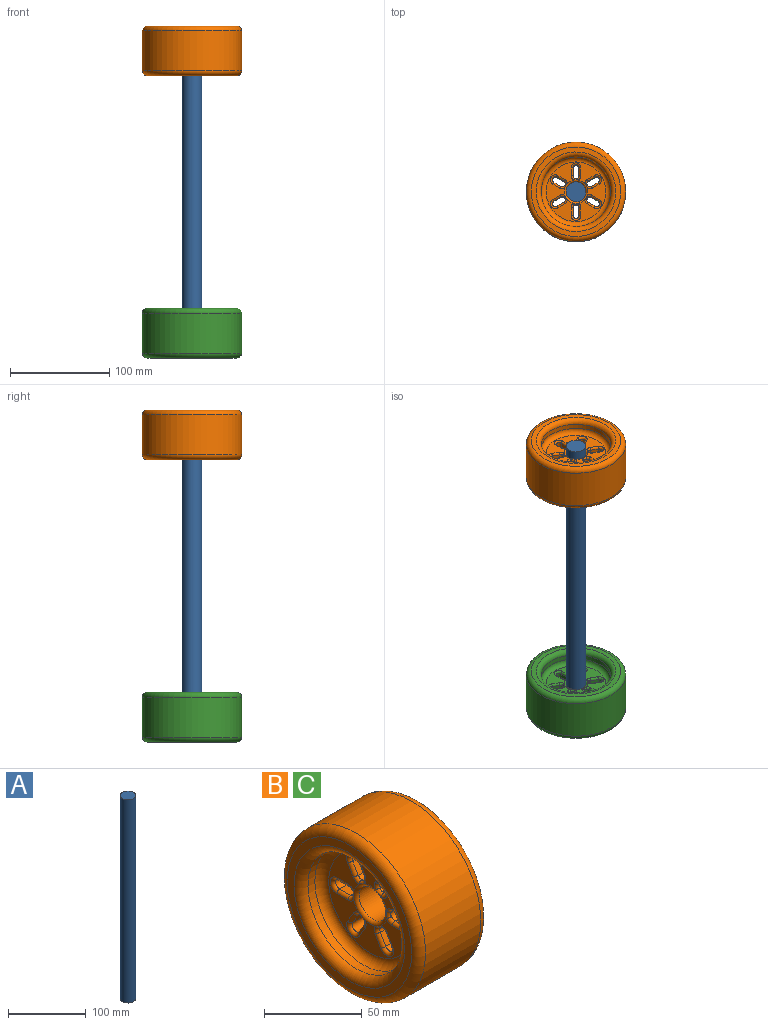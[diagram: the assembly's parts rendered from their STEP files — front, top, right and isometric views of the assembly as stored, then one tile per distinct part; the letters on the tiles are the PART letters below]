
ASSEMBLY  parts=3 mates=2
PART A: 3 faces, bbox 20x20x320 mm
  f0: cylinder r=10mm len=320mm, axis (0,0,-1), area 20106.2mm2, adj f1,f2
  f1: plane 20x20mm, normal (0,0,1), area 314.2mm2, adj f0
  f2: plane 20x20mm, normal (0,0,-1), area 314.2mm2, adj f0
PART B: 112 faces, bbox 50x108.2x108.2 mm
  f0: cylinder r=2mm len=7.93mm, axis (0,0.5,-0.87), area 25.1mm2, adj f1,f2,f15,f86
  f1: torus R=5mm, axis (1,0,0), area 36.8mm2, adj f0,f3,f12,f86
  f2: torus R=5mm, axis (1,0,0), area 12mm2, adj f0,f4,f14,f86
  f3: cylinder r=2mm len=7.93mm, axis (0,-0.5,0.87), area 25.1mm2, adj f1,f5,f13,f86
  f4: bspline ~5.09x4.08mm, area 9.2mm2, adj f2,f5,f14,f87
  f5: torus R=5mm, axis (1,0,0), area 12mm2, adj f3,f4,f14,f86
  f6: cylinder r=2mm len=7.93mm, axis (0,-0.5,0.87), area 25.1mm2, adj f7,f8,f15,f90
  f7: torus R=5mm, axis (1,0,0), area 36.8mm2, adj f6,f9,f12,f90
  f8: torus R=5mm, axis (1,0,0), area 12mm2, adj f6,f10,f14,f90
  f9: cylinder r=2mm len=7.93mm, axis (0,0.5,-0.87), area 25.1mm2, adj f7,f11,f13,f90
  f10: bspline ~5.09x4.08mm, area 9.2mm2, adj f8,f11,f14,f89
  f11: torus R=5mm, axis (1,0,0), area 12mm2, adj f9,f10,f14,f90
  f12: cylinder r=3mm len=16mm, axis (-1,0,0), area 150.8mm2, adj f1,f7,f13,f15
  f13: plane 16x6.93mm, normal (0,0.87,0.5), area 128mm2, adj f3,f9,f12,f14
  f14: cylinder r=3mm len=16mm, axis (-1,0,0), area 150.8mm2, adj f2,f4,f5,f8,f10,f11,f13,f15
  f15: plane 16x6.93mm, normal (0,-0.87,-0.5), area 128mm2, adj f0,f6,f12,f14
  f16: cylinder r=2mm len=7.93mm, axis (0,-0.5,-0.87), area 25.1mm2, adj f17,f18,f31,f86
  f17: torus R=5mm, axis (1,0,0), area 36.8mm2, adj f16,f19,f28,f86
  f18: torus R=5mm, axis (1,0,0), area 12mm2, adj f16,f20,f30,f86
  f19: cylinder r=2mm len=7.93mm, axis (0,0.5,0.87), area 25.1mm2, adj f17,f21,f29,f86
  f20: bspline ~4.47x3.55mm, area 9.2mm2, adj f18,f21,f30,f87
  f21: torus R=5mm, axis (1,0,0), area 12mm2, adj f19,f20,f30,f86
  f22: cylinder r=2mm len=7.93mm, axis (0,0.5,0.87), area 25.1mm2, adj f23,f24,f31,f90
  f23: torus R=5mm, axis (1,0,0), area 36.8mm2, adj f22,f25,f28,f90
  f24: torus R=5mm, axis (1,0,0), area 12mm2, adj f22,f26,f30,f90
  f25: cylinder r=2mm len=7.93mm, axis (0,-0.5,-0.87), area 25.1mm2, adj f23,f27,f29,f90
  f26: bspline ~4.47x3.55mm, area 9.2mm2, adj f24,f27,f30,f89
  f27: torus R=5mm, axis (1,0,0), area 12mm2, adj f25,f26,f30,f90
  f28: cylinder r=3mm len=16mm, axis (-1,0,0), area 150.8mm2, adj f17,f23,f29,f31
  f29: plane 16x6.93mm, normal (0,0.87,-0.5), area 128mm2, adj f19,f25,f28,f30
  f30: cylinder r=3mm len=16mm, axis (-1,0,0), area 150.8mm2, adj f18,f20,f21,f24,f26,f27,f29,f31
  f31: plane 16x6.93mm, normal (0,-0.87,0.5), area 128mm2, adj f16,f22,f28,f30
  f32: cylinder r=2mm len=8mm, axis (0,-1,0), area 25.1mm2, adj f33,f34,f47,f86
  f33: torus R=5mm, axis (1,0,0), area 36.8mm2, adj f32,f35,f44,f86
  f34: torus R=5mm, axis (1,0,0), area 12mm2, adj f32,f36,f46,f86
  f35: cylinder r=2mm len=8mm, axis (0,1,0), area 25.1mm2, adj f33,f37,f45,f86
  f36: bspline ~5.85x2.29mm, area 9.2mm2, adj f34,f37,f46,f87
  f37: torus R=5mm, axis (1,0,0), area 12mm2, adj f35,f36,f46,f86
  f38: cylinder r=2mm len=8mm, axis (0,1,0), area 25.1mm2, adj f39,f40,f47,f90
  f39: torus R=5mm, axis (1,0,0), area 36.8mm2, adj f38,f41,f44,f90
  f40: torus R=5mm, axis (1,0,0), area 12mm2, adj f38,f42,f46,f90
  f41: cylinder r=2mm len=8mm, axis (0,-1,0), area 25.1mm2, adj f39,f43,f45,f90
  f42: bspline ~5.85x2.29mm, area 9.2mm2, adj f40,f43,f46,f89
  f43: torus R=5mm, axis (1,0,0), area 12mm2, adj f41,f42,f46,f90
  f44: cylinder r=3mm len=16mm, axis (-1,0,0), area 150.8mm2, adj f33,f39,f45,f47
  f45: plane 16x8mm, normal (0,0,-1), area 128mm2, adj f35,f41,f44,f46
  f46: cylinder r=3mm len=16mm, axis (-1,0,0), area 150.8mm2, adj f34,f36,f37,f40,f42,f43,f45,f47
  f47: plane 16x8mm, normal (0,0,1), area 128mm2, adj f32,f38,f44,f46
  f48: cylinder r=2mm len=7.93mm, axis (0,-0.5,0.87), area 25.1mm2, adj f49,f50,f63,f86
  f49: torus R=5mm, axis (1,0,0), area 36.8mm2, adj f48,f51,f60,f86
  f50: torus R=5mm, axis (1,0,0), area 12mm2, adj f48,f52,f62,f86
  f51: cylinder r=2mm len=7.93mm, axis (0,0.5,-0.87), area 25.1mm2, adj f49,f53,f61,f86
  f52: bspline ~5.09x4.08mm, area 9.2mm2, adj f50,f53,f62,f87
  f53: torus R=5mm, axis (1,0,0), area 12mm2, adj f51,f52,f62,f86
  f54: cylinder r=2mm len=7.93mm, axis (0,0.5,-0.87), area 25.1mm2, adj f55,f56,f63,f90
  f55: torus R=5mm, axis (1,0,0), area 36.8mm2, adj f54,f57,f60,f90
  f56: torus R=5mm, axis (1,0,0), area 12mm2, adj f54,f58,f62,f90
  f57: cylinder r=2mm len=7.93mm, axis (0,-0.5,0.87), area 25.1mm2, adj f55,f59,f61,f90
  f58: bspline ~5.09x4.08mm, area 9.2mm2, adj f56,f59,f62,f89
  f59: torus R=5mm, axis (1,0,0), area 12mm2, adj f57,f58,f62,f90
  f60: cylinder r=3mm len=16mm, axis (-1,0,0), area 150.8mm2, adj f49,f55,f61,f63
  f61: plane 16x6.93mm, normal (0,-0.87,-0.5), area 128mm2, adj f51,f57,f60,f62
  f62: cylinder r=3mm len=16mm, axis (-1,0,0), area 150.8mm2, adj f50,f52,f53,f56,f58,f59,f61,f63
  f63: plane 16x6.93mm, normal (0,0.87,0.5), area 128mm2, adj f48,f54,f60,f62
  f64: cylinder r=2mm len=7.93mm, axis (0,0.5,0.87), area 25.1mm2, adj f65,f66,f79,f86
  f65: torus R=5mm, axis (1,0,0), area 36.8mm2, adj f64,f67,f76,f86
  f66: torus R=5mm, axis (1,0,0), area 12mm2, adj f64,f68,f78,f86
  f67: cylinder r=2mm len=7.93mm, axis (0,-0.5,-0.87), area 25.1mm2, adj f65,f69,f77,f86
  f68: bspline ~4.47x3.55mm, area 9.2mm2, adj f66,f69,f78,f87
  f69: torus R=5mm, axis (1,0,0), area 12mm2, adj f67,f68,f78,f86
  f70: cylinder r=2mm len=7.93mm, axis (0,-0.5,-0.87), area 25.1mm2, adj f71,f72,f79,f90
  f71: torus R=5mm, axis (1,0,0), area 36.8mm2, adj f70,f73,f76,f90
  f72: torus R=5mm, axis (1,0,0), area 12mm2, adj f70,f74,f78,f90
  f73: cylinder r=2mm len=7.93mm, axis (0,0.5,0.87), area 25.1mm2, adj f71,f75,f77,f90
  f74: bspline ~4.47x3.55mm, area 9.2mm2, adj f72,f75,f78,f89
  f75: torus R=5mm, axis (1,0,0), area 12mm2, adj f73,f74,f78,f90
  f76: cylinder r=3mm len=16mm, axis (-1,0,0), area 150.8mm2, adj f65,f71,f77,f79
  f77: plane 16x6.93mm, normal (0,-0.87,0.5), area 128mm2, adj f67,f73,f76,f78
  f78: cylinder r=3mm len=16mm, axis (-1,0,0), area 150.8mm2, adj f66,f68,f69,f72,f74,f75,f77,f79
  f79: plane 16x6.93mm, normal (0,0.87,-0.5), area 128mm2, adj f64,f70,f76,f78
  f80: cylinder r=50mm len=100mm, axis (-1,0,0), area 12566.4mm2, adj f81,f95
  f81: torus R=45mm, axis (-1,0,0), area 2377.7mm2, adj f80,f82
  f82: plane 90x90mm, normal (-1,0,0), area 1335.2mm2, adj f81,f83
  f83: torus R=40mm, axis (-1,0,0), area 1816.8mm2, adj f82,f84
  f84: cylinder r=35mm len=70mm, axis (-1,0,0), area 1099.6mm2, adj f83,f85
  f85: torus R=30mm, axis (-1,0,0), area 1637.5mm2, adj f84,f86
  f86: plane 60x60mm, normal (-1,0,0), area 1444.7mm2, adj f0,f1,f2,f3,f5,f16,f17,f18
  f87: torus R=12mm, axis (-1,0,0), area 211.7mm2, adj f4,f20,f36,f52,f68,f86,f88,f110
  f88: cylinder r=10mm len=20mm, axis (-1,0,0), area 1005.3mm2, adj f87,f89
  f89: torus R=12mm, axis (-1,0,0), area 211.7mm2, adj f10,f26,f42,f58,f74,f88,f90,f104
  f90: plane 60x60mm, normal (1,0,0), area 1444.7mm2, adj f6,f7,f8,f9,f11,f22,f23,f24
  f91: torus R=30mm, axis (-1,0,0), area 1637.5mm2, adj f90,f92
  f92: cylinder r=35mm len=70mm, axis (-1,0,0), area 1099.6mm2, adj f91,f93
  f93: torus R=40mm, axis (-1,0,0), area 1816.8mm2, adj f92,f94
  f94: plane 90x90mm, normal (1,0,0), area 1335.2mm2, adj f93,f95
  f95: torus R=45mm, axis (-1,0,0), area 2377.7mm2, adj f80,f94
  f96: cylinder r=3mm len=16mm, axis (-1,0,0), area 150.8mm2, adj f97,f99,f101,f107
  f97: plane 16x8mm, normal (0,0,1), area 128mm2, adj f96,f98,f103,f109
  f98: cylinder r=3mm len=16mm, axis (-1,0,0), area 150.8mm2, adj f97,f99,f102,f104,f105,f108,f110,f111
  f99: plane 16x8mm, normal (0,0,-1), area 128mm2, adj f96,f98,f100,f106
  f100: cylinder r=2mm len=8mm, axis (0,-1,0), area 25.1mm2, adj f90,f99,f101,f102
  f101: torus R=5mm, axis (1,0,0), area 36.8mm2, adj f90,f96,f100,f103
  f102: torus R=5mm, axis (1,0,0), area 12mm2, adj f90,f98,f100,f104
  f103: cylinder r=2mm len=8mm, axis (0,1,0), area 25.1mm2, adj f90,f97,f101,f105
  f104: bspline ~5.85x2.29mm, area 9.2mm2, adj f89,f98,f102,f105
  f105: torus R=5mm, axis (1,0,0), area 12mm2, adj f90,f98,f103,f104
  f106: cylinder r=2mm len=8mm, axis (0,1,0), area 25.1mm2, adj f86,f99,f107,f108
  f107: torus R=5mm, axis (1,0,0), area 36.8mm2, adj f86,f96,f106,f109
  f108: torus R=5mm, axis (1,0,0), area 12mm2, adj f86,f98,f106,f110
  f109: cylinder r=2mm len=8mm, axis (0,-1,0), area 25.1mm2, adj f86,f97,f107,f111
  f110: bspline ~5.85x2.29mm, area 9.2mm2, adj f87,f98,f108,f111
  f111: torus R=5mm, axis (1,0,0), area 12mm2, adj f86,f98,f109,f110
PART C: same geometry as B
PLACE A t=(-441.9,-105.14,-92.65)mm fixed
PLACE B rot(axis=(0.71,0,0.71),180deg) t=(-441.9,-103.77,209.35)mm
PLACE C rot(axis=(0,-1,0),90deg) t=(-441.9,-103.77,-74.65)mm
MATE fastened A.f0 <-> C.f80  axis (0,0,-1) through (-441.9,-103.77,-92.65)mm
MATE fastened A.f0 <-> B.f80  axis (0,0,1) through (-441.9,-103.77,227.35)mm
